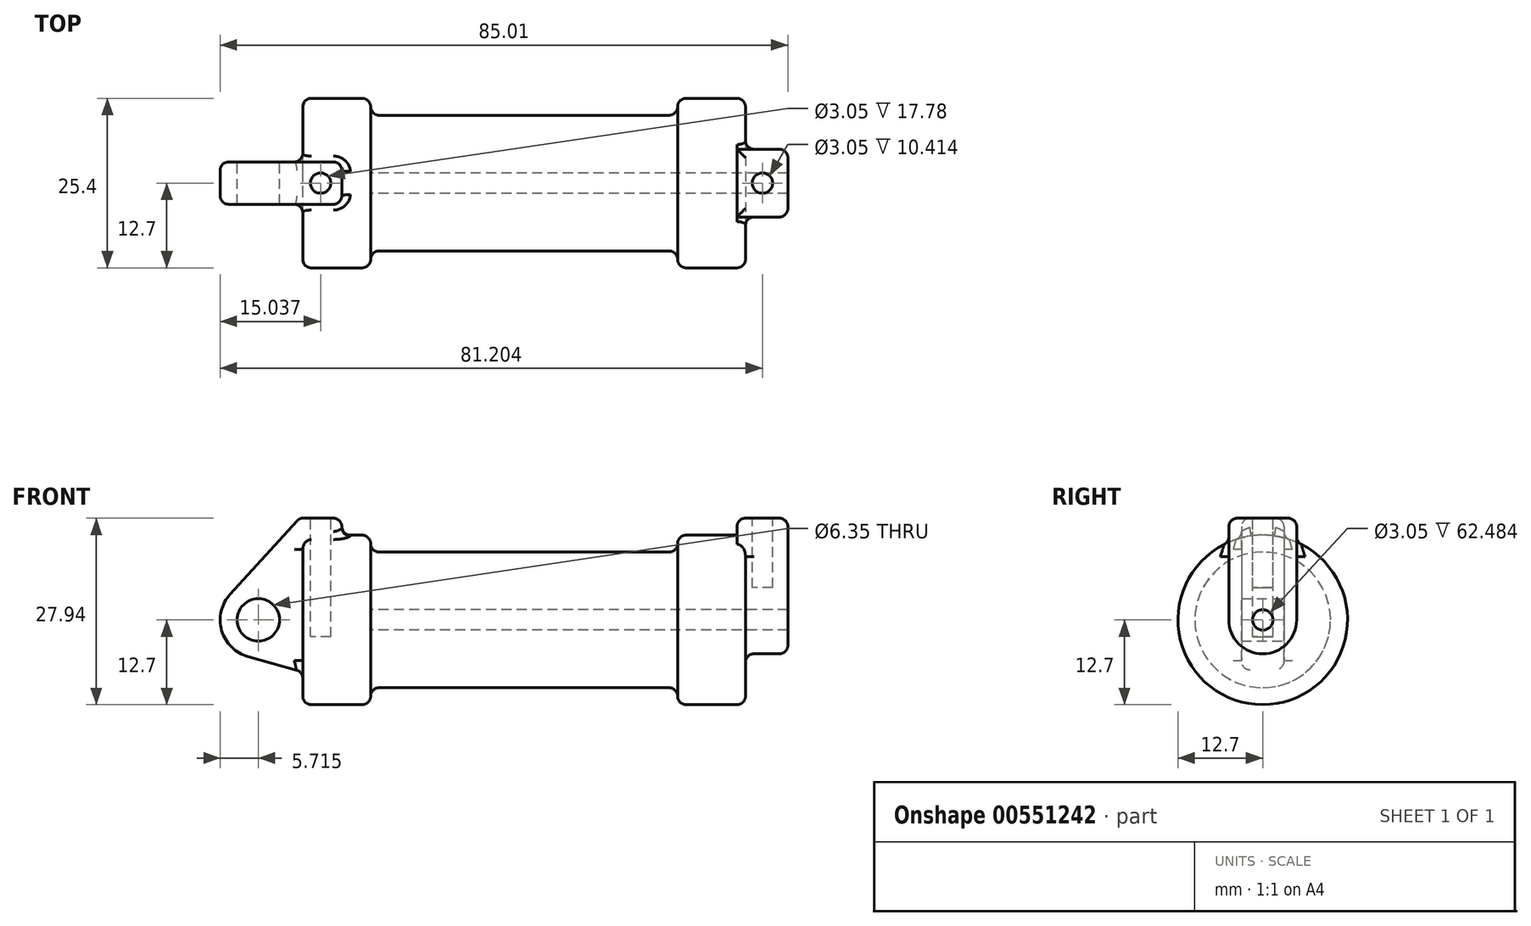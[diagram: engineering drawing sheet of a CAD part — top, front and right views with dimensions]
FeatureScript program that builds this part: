
annotation { "Feature Type Name" : "Feature", "Feature Type Description" : "" }
export const myFeature = defineFeature(function(context is Context, id is Id, definition is map)
    precondition{}
    {
        {
            var Q0;
            Q0=qCreatedBy(makeId("Front.planeOp"),FACE);
            var sketch = newSketch(context, id + "F0", { "sketchPlane" : qUnion([Q0])});
            skLineSegment(sketch, "E0", {"start": v(0, 0) * mm, "end": v(0, 12.7) * mm});
            skLineSegment(sketch, "E1", {"start": v(0, 12.7) * mm, "end": v(10.16, 12.7) * mm});
            skLineSegment(sketch, "E2", {"start": v(10.16, 12.7) * mm, "end": v(10.16, 10.16) * mm});
            skLineSegment(sketch, "E3", {"start": v(10.16, 10.16) * mm, "end": v(56.13, 10.16) * mm});
            skLineSegment(sketch, "E4", {"start": v(56.13, 10.16) * mm, "end": v(56.13, 12.7) * mm});
            skLineSegment(sketch, "E5", {"start": v(56.13, 12.7) * mm, "end": v(66.3, 12.7) * mm});
            skLineSegment(sketch, "E6", {"start": v(66.3, 12.7) * mm, "end": v(66.3, 0) * mm});
            skLineSegment(sketch, "E7", {"start": v(66.3, 0) * mm, "end": v(0, 0) * mm});
            skLineSegment(sketch, "E8", {"start": v(5.84, 15.24) * mm, "end": v(-0.5, 15.24) * mm});
            skLineSegment(sketch, "E9", {"start": v(-0.5, 15.24) * mm, "end": v(-10.88, 3.85) * mm});
            skLineSegment(sketch, "E10", {"start": v(0, 0) * mm, "end": v(-6.65, 0) * mm});
            skCircle(sketch, "E11", {"center": v(-6.65, 0) * mm, "radius": 5.72 * mm});
            skCircle(sketch, "E12", {"center": v(-6.65, 0) * mm, "radius": 3.18 * mm});
            skLineSegment(sketch, "E13", {"start": v(5.84, 15.24) * mm, "end": v(5.84, -9.4) * mm});
            skLineSegment(sketch, "E14", {"start": v(5.84, -9.4) * mm, "end": v(-8.18, -5.5) * mm});
            skSolve(sketch);
        }
        {
            var Q0;
            {var subQ0=sQuery(id+"F0.wireOp",EDGE,"E2");Q0=makeQuery(id+"F0.imprint","IMPRINT",FACE,{"disambiguationData":[TD([[makeQuery(id+"F0.imprint","IMPRINT",EDGE,{"derivedFrom":subQ0}),-1.0]])]});}
            var Q1;
            {var subQ0=sQuery(id+"F0.wireOp",EDGE,"E0");Q1=makeQuery(id+"F0.imprint","IMPRINT",FACE,{"disambiguationData":[TD([[makeQuery(id+"F0.imprint","IMPRINT",EDGE,{"derivedFrom":subQ0}),-1.0]])]});}
            var Q2;
            Q2=sQuery(id+"F0.wireOp",EDGE,"E7");
            revolve(context, id + "F1", {"entities" : qUnion([Q0, Q1]), "axis" : qUnion([Q2]), "revolveType" : RevolveType.FULL});
        }
        {
            var Q0;
            {var subQ3=sQuery(id+"F0.wireOp",EDGE,"E0");Q0=makeQuery(id+"F0.imprint","IMPRINT",FACE,{"disambiguationData":[TD([[makeQuery(id+"F0.imprint","IMPRINT",EDGE,{"derivedFrom":subQ3}),1.0]])]});}
            var Q1;
            {var subQ4=sQuery(id+"F0.wireOp",EDGE,"E12");Q1=makeQuery(id+"F0.imprint","IMPRINT",FACE,{"disambiguationData":[TD([[makeQuery(id+"F0.imprint","IMPRINT",EDGE,{"derivedFrom":subQ4}),-1.0]])]});}
            var Q2;
            {var subQ0=sQuery(id+"F0.wireOp",EDGE,"E14");Q2=makeQuery(id+"F0.imprint","IMPRINT",FACE,{"disambiguationData":[TD([[makeQuery(id+"F0.imprint","IMPRINT",EDGE,{"derivedFrom":subQ0}),-1.0]])]});}
            var Q3;
            {var subQ0=sQuery(id+"F0.wireOp",EDGE,"E0");Q3=makeQuery(id+"F0.imprint","IMPRINT",FACE,{"disambiguationData":[TD([[makeQuery(id+"F0.imprint","IMPRINT",EDGE,{"derivedFrom":subQ0}),-1.0]])]});}
            extrude(context, id + "F2", {"entities" : qUnion([Q0, Q1, Q2, Q3]), "operationType" : NewBodyOperationType.ADD, "endBound" : BoundingType.SYMMETRIC, "depth" : 6.35 * mm});
        }
        {
            var Q0;
            Q0=makeQuery(id+"F1.opRevolve","SWEPT_FACE",FACE,{"disambiguationData":[OSD([sQuery(id+"F0.wireOp",EDGE,"E6")])]});
            var sketch = newSketch(context, id + "F3", { "sketchPlane" : qUnion([Q0])});
            skCircle(sketch, "E15", {"center": v(0, 0) * mm, "radius": 1.52 * mm});
            skCircle(sketch, "E16", {"center": v(0, 0) * mm, "radius": 5.08 * mm});
            skLineSegment(sketch, "E17", {"start": v(-5.08, 0) * mm, "end": v(-5.08, 15.24) * mm});
            skLineSegment(sketch, "E18", {"start": v(-5.08, 15.24) * mm, "end": v(5.08, 15.24) * mm});
            skLineSegment(sketch, "E19", {"start": v(5.08, 15.24) * mm, "end": v(5.08, 0) * mm});
            skSolve(sketch);
        }
        {
            var Q0;
            {var subQ0=sQuery(id+"F3.wireOp",EDGE,"E18");Q0=makeQuery(id+"F3.imprint","IMPRINT",FACE,{"disambiguationData":[TD([[makeQuery(id+"F3.imprint","IMPRINT",EDGE,{"derivedFrom":subQ0}),-1.0]])]});}
            extrude(context, id + "F4", {"entities" : qUnion([Q0]), "operationType" : NewBodyOperationType.ADD, "oppositeDirection" : true, "depth" : 1.27 * mm});
        }
        {
            var Q0;
            {var subQ0=sQuery(id+"F3.wireOp",EDGE,"E18");Q0=makeQuery(id+"F3.imprint","IMPRINT",FACE,{"disambiguationData":[TD([[makeQuery(id+"F3.imprint","IMPRINT",EDGE,{"derivedFrom":subQ0}),-1.0]])]});}
            var Q1;
            {var subQ0=sQuery(id+"F3.wireOp",EDGE,"E17");var subQ1=sQuery(id+"F3.wireOp",EDGE,"E16");var subQ2=makeQuery(id+"F3.imprint","INTERSECT",VERTEX,{"derivedFrom":[subQ1,subQ0]});Q1=makeQuery(id+"F3.imprint","IMPRINT",FACE,{"disambiguationData":[TD([[makeQuery(id+"F3.imprint","IMPRINT",EDGE,{"disambiguationData":[TD([[subQ2,1.0]])],"derivedFrom":subQ1}),-1.0]])]});}
            var Q2;
            Q2=makeQuery(id+"F3.imprint","IMPRINT",FACE,{"disambiguationData":[TD([[makeQuery(id+"F3.imprint","IMPRINT",EDGE,{"derivedFrom":sQuery(id+"F3.wireOp",EDGE,"E15")}),-1.0]])]});
            extrude(context, id + "F5", {"entities" : qUnion([Q0, Q1, Q2]), "operationType" : NewBodyOperationType.ADD, "depth" : 6.35 * mm});
        }
        {
            var Q0;
            Q0=makeQuery(id+"F3.imprint","IMPRINT",FACE,{"disambiguationData":[TD([[makeQuery(id+"F3.imprint","IMPRINT",EDGE,{"derivedFrom":sQuery(id+"F3.wireOp",EDGE,"E15")}),1.0]])]});
            var Q1;
            Q1=makeQuery(id+"F1.opRevolve","SWEPT_FACE",FACE,{"disambiguationData":[OSD([sQuery(id+"F0.wireOp",EDGE,"E2")])]});
            extrude(context, id + "F6", {"entities" : qUnion([Q0]), "operationType" : NewBodyOperationType.REMOVE, "endBound" : BoundingType.UP_TO_SURFACE, "oppositeDirection" : true, "endBoundEntityFace" : qUnion([Q1]), "depth" : 25.4 * mm, "offsetDistance" : 25.4 * mm});
        }
        {
            var Q0;
            Q0=makeQuery(id+"F2.opExtrude","SWEPT_FACE",FACE,{"disambiguationData":[OSD([sQuery(id+"F0.wireOp",EDGE,"E8")])]});
            var sketch = newSketch(context, id + "F7", { "sketchPlane" : qUnion([Q0])});
            skCircle(sketch, "E20", {"center": v(2.67, 0) * mm, "radius": 1.52 * mm});
            skPoint(sketch, "E20.centerSnap0", {"position": v(-0.5, 0) * mm});
            skPoint(sketch, "E20.centerSnap1", {"position": v(2.67, 3.18) * mm});
            skSolve(sketch);
        }
        {
            var Q0;
            Q0=qSketchRegion(id+"F7",true);
            extrude(context, id + "F8", {"entities" : qUnion([Q0]), "operationType" : NewBodyOperationType.REMOVE, "oppositeDirection" : true, "depth" : 17.78 * mm, "offsetDistance" : 25.4 * mm});
        }
        {
            var Q0;
            {var subQ0=sQuery(id+"F3.wireOp",EDGE,"E18");Q0=makeQuery(id+"F5.boolean.opBoolean","MERGE",FACE,{"derivedFrom":[makeQuery(id+"F4.opExtrude","SWEPT_FACE",FACE,{"disambiguationData":[OSD([subQ0])]}),makeQuery(id+"F5.opExtrude","SWEPT_FACE",FACE,{"disambiguationData":[OSD([subQ0])]})]});}
            var sketch = newSketch(context, id + "F9", { "sketchPlane" : qUnion([Q0])});
            skCircle(sketch, "E21", {"center": v(68.83, 0) * mm, "radius": 1.52 * mm});
            skPoint(sketch, "E21.centerSnap0", {"position": v(65.02, 0) * mm});
            skPoint(sketch, "E21.centerSnap1", {"position": v(68.83, 5.08) * mm});
            skSolve(sketch);
        }
        {
            var Q0;
            Q0=qSketchRegion(id+"F9",true);
            extrude(context, id + "F10", {"entities" : qUnion([Q0]), "operationType" : NewBodyOperationType.REMOVE, "oppositeDirection" : true, "depth" : 10.4 * mm});
        }
        {
            var Q0;
            Q0=makeQuery(id+"F1.opRevolve","SWEPT_EDGE",EDGE,{"disambiguationData":[OSD([sQuery(id+"F0.wireOp",EDGE,"E2"),sQuery(id+"F0.wireOp",EDGE,"E3")])]});
            var Q1;
            Q1=makeQuery(id+"F1.opRevolve","SWEPT_EDGE",EDGE,{"disambiguationData":[OSD([sQuery(id+"F0.wireOp",EDGE,"E1"),sQuery(id+"F0.wireOp",EDGE,"E2")])]});
            var Q2;
            Q2=makeQuery(id+"F1.opRevolve","SWEPT_EDGE",EDGE,{"disambiguationData":[OSD([sQuery(id+"F0.wireOp",EDGE,"E3"),sQuery(id+"F0.wireOp",EDGE,"E4")])]});
            var Q3;
            Q3=makeQuery(id+"F1.opRevolve","SWEPT_EDGE",EDGE,{"disambiguationData":[OSD([sQuery(id+"F0.wireOp",EDGE,"E4"),sQuery(id+"F0.wireOp",EDGE,"E5")])]});
            var Q4;
            Q4=makeQuery(id+"F1.opRevolve","SWEPT_EDGE",EDGE,{"disambiguationData":[OSD([sQuery(id+"F0.wireOp",EDGE,"E5"),sQuery(id+"F0.wireOp",EDGE,"E6")])]});
            var Q5;
            Q5=makeQuery(id+"F1.opRevolve","SWEPT_EDGE",EDGE,{"disambiguationData":[OSD([sQuery(id+"F0.wireOp",EDGE,"E0"),sQuery(id+"F0.wireOp",EDGE,"E1")])]});
            fillet(context, id + "F11", {"entities" : qUnion([Q0, Q1, Q2, Q3, Q4, Q5]), "radius" : 1.27 * mm, "tangentPropagation" : true, "allowEdgeOverflow" : false});
        }
        {
            var Q0;
            Q0=makeQuery(id+"F1.boolean.opBoolean","INTERSECT",EDGE,{"derivedFrom":[makeQuery(id+"F2.opExtrude","CAP_FACE",FACE,{"disambiguationData":[OSD([sQuery(id+"F0.wireOp",EDGE,"E8"),sQuery(id+"F0.wireOp",EDGE,"E9"),sQuery(id+"F0.wireOp",EDGE,"E11"),sQuery(id+"F0.wireOp",EDGE,"E12"),sQuery(id+"F0.wireOp",EDGE,"E13"),sQuery(id+"F0.wireOp",EDGE,"E14")])],"isStart":false}),makeQuery(id+"F1.opRevolve","SWEPT_FACE",FACE,{"disambiguationData":[OSD([sQuery(id+"F0.wireOp",EDGE,"E1")])]})]});
            var Q1;
            Q1=makeQuery(id+"F1.opRevolve","SWEPT_FACE",FACE,{"disambiguationData":[OSD([sQuery(id+"F0.wireOp",EDGE,"E0")])]});
            var Q2;
            Q2=makeQuery(id+"F2.opExtrude","CAP_EDGE",EDGE,{"disambiguationData":[OSD([sQuery(id+"F0.wireOp",EDGE,"E9")])],"isStart":true});
            var Q3;
            Q3=makeQuery(id+"F2.opExtrude","CAP_EDGE",EDGE,{"disambiguationData":[OSD([sQuery(id+"F0.wireOp",EDGE,"E9")])],"isStart":false});
            var Q4;
            Q4=makeQuery(id+"F5.opExtrude","CAP_EDGE",EDGE,{"disambiguationData":[OSD([sQuery(id+"F3.wireOp",EDGE,"E17")])],"isStart":true});
            var Q5;
            Q5=makeQuery(id+"F5.opExtrude","CAP_EDGE",EDGE,{"disambiguationData":[OSD([sQuery(id+"F3.wireOp",EDGE,"E17")])],"isStart":false});
            var Q6;
            {var subQ0=sQuery(id+"F3.wireOp",EDGE,"E18");var subQ1=sQuery(id+"F3.wireOp",EDGE,"E17");Q6=makeQuery(id+"F5.boolean.opBoolean","MERGE",EDGE,{"derivedFrom":[makeQuery(id+"F4.opExtrude","SWEPT_EDGE",EDGE,{"disambiguationData":[OSD([subQ1,subQ0])]}),makeQuery(id+"F5.opExtrude","SWEPT_EDGE",EDGE,{"disambiguationData":[OSD([subQ1,subQ0])]})]});}
            var Q7;
            {var subQ0=sQuery(id+"F3.wireOp",EDGE,"E19");var subQ1=sQuery(id+"F3.wireOp",EDGE,"E18");Q7=makeQuery(id+"F5.boolean.opBoolean","MERGE",EDGE,{"derivedFrom":[makeQuery(id+"F4.opExtrude","SWEPT_EDGE",EDGE,{"disambiguationData":[OSD([subQ1,subQ0])]}),makeQuery(id+"F5.opExtrude","SWEPT_EDGE",EDGE,{"disambiguationData":[OSD([subQ1,subQ0])]})]});}
            var Q8;
            Q8=makeQuery(id+"F4.opExtrude","CAP_EDGE",EDGE,{"disambiguationData":[OSD([sQuery(id+"F3.wireOp",EDGE,"E18")])],"isStart":false});
            var Q9;
            Q9=makeQuery(id+"F5.opExtrude","CAP_EDGE",EDGE,{"disambiguationData":[OSD([sQuery(id+"F3.wireOp",EDGE,"E18")])],"isStart":false});
            var Q10;
            Q10=makeQuery(id+"F2.opExtrude","CAP_EDGE",EDGE,{"disambiguationData":[OSD([sQuery(id+"F0.wireOp",EDGE,"E8")])],"isStart":false});
            var Q11;
            Q11=makeQuery(id+"F2.opExtrude","SWEPT_EDGE",EDGE,{"disambiguationData":[OSD([sQuery(id+"F0.wireOp",EDGE,"E8"),sQuery(id+"F0.wireOp",EDGE,"E9")])]});
            var Q12;
            Q12=makeQuery(id+"F2.opExtrude","CAP_EDGE",EDGE,{"disambiguationData":[OSD([sQuery(id+"F0.wireOp",EDGE,"E8")])],"isStart":true});
            var Q13;
            Q13=makeQuery(id+"F2.opExtrude","SWEPT_EDGE",EDGE,{"disambiguationData":[OSD([sQuery(id+"F0.wireOp",EDGE,"E8"),sQuery(id+"F0.wireOp",EDGE,"E13")])]});
            var Q14;
            Q14=makeQuery(id+"F2.opExtrude","SWEPT_FACE",FACE,{"disambiguationData":[OSD([sQuery(id+"F0.wireOp",EDGE,"E13")])]});
            var Q15;
            Q15=makeQuery(id+"F4.opExtrude","CAP_EDGE",EDGE,{"disambiguationData":[OSD([sQuery(id+"F0.wireOp",EDGE,"E5"),sQuery(id+"F0.wireOp",EDGE,"E6")])],"isStart":false});
            fillet(context, id + "F12", {"entities" : qUnion([Q0, Q1, Q2, Q3, Q4, Q5, Q6, Q7, Q8, Q9, Q10, Q11, Q12, Q13, Q14, Q15]), "radius" : 1.27 * mm, "tangentPropagation" : true, "allowEdgeOverflow" : false});
        }
    });
